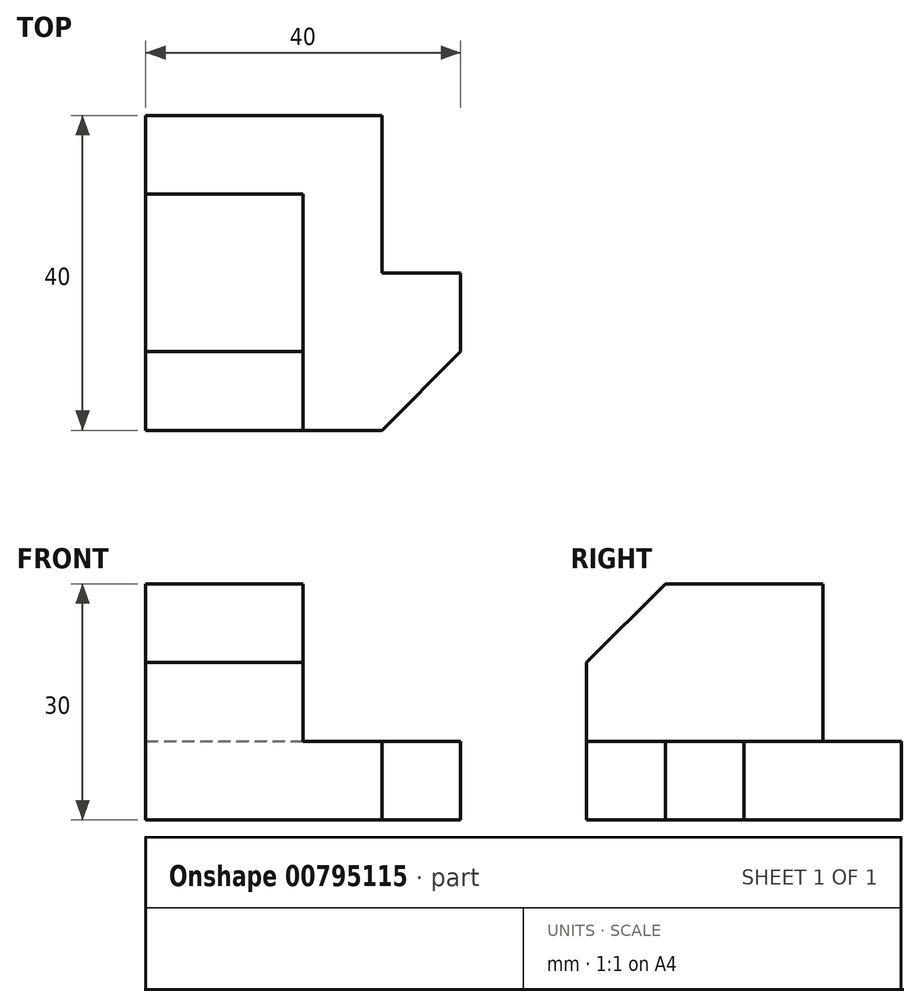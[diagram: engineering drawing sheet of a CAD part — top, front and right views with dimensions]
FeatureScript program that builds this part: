
annotation { "Feature Type Name" : "Feature", "Feature Type Description" : "" }
export const myFeature = defineFeature(function(context is Context, id is Id, definition is map)
    precondition{}
    {
        {
            var Q0;
            Q0=qCreatedBy(makeId("Top.planeOp"),FACE);
            var sketch = newSketch(context, id + "F0", { "sketchPlane" : qUnion([Q0])});
            skLineSegment(sketch, "E0", {"start": v(-15.38, 7.67) * mm, "end": v(14.62, 7.67) * mm});
            skLineSegment(sketch, "E1", {"start": v(14.62, 7.67) * mm, "end": v(14.62, -12.33) * mm});
            skLineSegment(sketch, "E2", {"start": v(14.62, -12.33) * mm, "end": v(24.62, -12.33) * mm});
            skLineSegment(sketch, "E3", {"start": v(24.62, -12.33) * mm, "end": v(24.62, -22.33) * mm});
            skLineSegment(sketch, "E4", {"start": v(24.62, -22.33) * mm, "end": v(14.62, -32.33) * mm});
            skLineSegment(sketch, "E5", {"start": v(14.62, -32.33) * mm, "end": v(-15.38, -32.33) * mm});
            skLineSegment(sketch, "E6", {"start": v(-15.38, -32.33) * mm, "end": v(-15.38, 7.67) * mm});
            skSolve(sketch);
        }
        {
            var Q0;
            Q0=makeQuery(id+"F0.imprint","IMPRINT",FACE,{"disambiguationData":[TD([[makeQuery(id+"F0.imprint","IMPRINT",EDGE,{"derivedFrom":sQuery(id+"F0.wireOp",EDGE,"E0")}),-1.0]])]});
            extrude(context, id + "F1", {"entities" : qUnion([Q0]), "depth" : 10 * mm, "offsetDistance" : 25 * mm});
        }
        {
            var Q0;
            Q0=makeQuery(id+"F1.opExtrude","SWEPT_FACE",FACE,{"disambiguationData":[OSD([sQuery(id+"F0.wireOp",EDGE,"E6")])]});
            var sketch = newSketch(context, id + "F2", { "sketchPlane" : qUnion([Q0])});
            skLineSegment(sketch, "E7", {"start": v(32.33, 10) * mm, "end": v(2.33, 10) * mm});
            skLineSegment(sketch, "E8", {"start": v(2.33, 10) * mm, "end": v(2.33, 30) * mm});
            skLineSegment(sketch, "E9", {"start": v(2.33, 30) * mm, "end": v(22.33, 30) * mm});
            skLineSegment(sketch, "E10", {"start": v(22.33, 30) * mm, "end": v(32.33, 20) * mm});
            skLineSegment(sketch, "E11", {"start": v(32.33, 20) * mm, "end": v(32.33, 10) * mm});
            skSolve(sketch);
        }
        {
            var Q0;
            Q0=makeQuery(id+"F2.imprint","IMPRINT",FACE,{"disambiguationData":[TD([[makeQuery(id+"F2.imprint","IMPRINT",EDGE,{"derivedFrom":sQuery(id+"F2.wireOp",EDGE,"E7")}),-1.0]])]});
            extrude(context, id + "F3", {"entities" : qUnion([Q0]), "operationType" : NewBodyOperationType.ADD, "oppositeDirection" : true, "depth" : 20 * mm, "offsetDistance" : 25 * mm});
        }
    });
